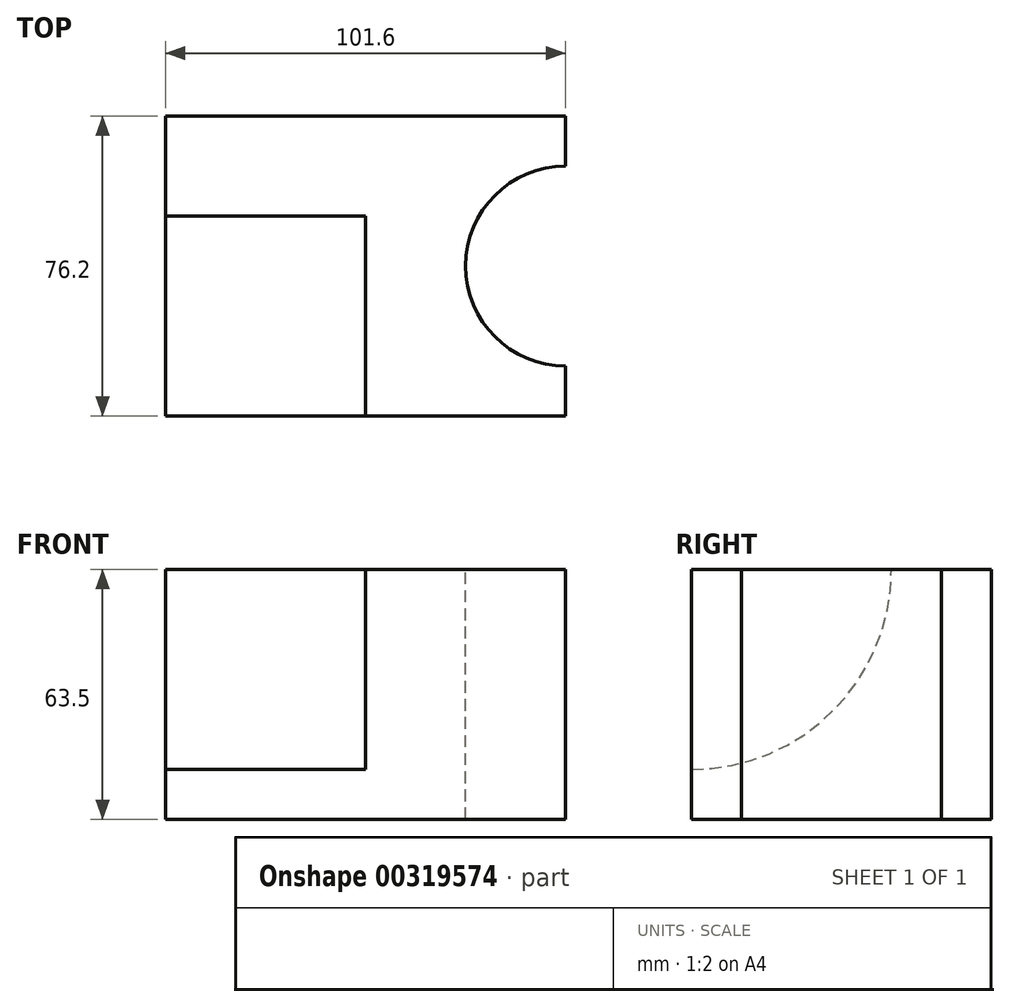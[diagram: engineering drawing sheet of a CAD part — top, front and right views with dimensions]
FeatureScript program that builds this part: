
annotation { "Feature Type Name" : "Feature", "Feature Type Description" : "" }
export const myFeature = defineFeature(function(context is Context, id is Id, definition is map)
    precondition{}
    {
        {
            var Q0;
            Q0=qCreatedBy(makeId("Front.planeOp"),FACE);
            var sketch = newSketch(context, id + "F0", { "sketchPlane" : qUnion([Q0])});
            skLineSegment(sketch, "E0", {"start": v(-45.54, -62.06) * mm, "end": v(56.06, -62.06) * mm});
            skLineSegment(sketch, "E1", {"start": v(-45.54, -62.06) * mm, "end": v(-45.54, 1.44) * mm});
            skLineSegment(sketch, "E2", {"start": v(-45.54, 1.44) * mm, "end": v(56.06, 1.44) * mm});
            skLineSegment(sketch, "E3", {"start": v(56.06, 1.44) * mm, "end": v(56.06, -62.06) * mm});
            skSolve(sketch);
        }
        {
            var Q0;
            Q0=makeQuery(id+"F0.imprint","IMPRINT",FACE,{"disambiguationData":[TD([[makeQuery(id+"F0.imprint","IMPRINT",EDGE,{"derivedFrom":sQuery(id+"F0.wireOp",EDGE,"E0")}),1.0]])]});
            extrude(context, id + "F1", {"entities" : qUnion([Q0]), "depth" : 76.2 * mm});
        }
        {
            var Q0;
            Q0=makeQuery(id+"F1.opExtrude","SWEPT_FACE",FACE,{"disambiguationData":[OSD([sQuery(id+"F0.wireOp",EDGE,"E2")])]});
            var sketch = newSketch(context, id + "F2", { "sketchPlane" : qUnion([Q0])});
            skArc(sketch, "E4", {"start": v(56.06, -12.7) * mm, "mid": v(30.66, -38.1) * mm, "end": v(56.06, -63.5) * mm});
            skLineSegment(sketch, "E5", {"start": v(56.06, -63.5) * mm, "end": v(56.06, -12.7) * mm});
            skSolve(sketch);
        }
        {
            var Q0;
            Q0=makeQuery(id+"F2.imprint","IMPRINT",FACE,{"disambiguationData":[TD([[makeQuery(id+"F2.imprint","IMPRINT",EDGE,{"derivedFrom":sQuery(id+"F2.wireOp",EDGE,"E4")}),1.0]])]});
            extrude(context, id + "F3", {"entities" : qUnion([Q0]), "operationType" : NewBodyOperationType.REMOVE, "oppositeDirection" : true, "depth" : 63.5 * mm});
        }
        {
            var Q0;
            Q0=makeQuery(id+"F1.opExtrude","SWEPT_FACE",FACE,{"disambiguationData":[OSD([sQuery(id+"F0.wireOp",EDGE,"E1")])]});
            var sketch = newSketch(context, id + "F4", { "sketchPlane" : qUnion([Q0])});
            skArc(sketch, "E6", {"start": v(25.4, 1.44) * mm, "mid": v(40.28, -34.48) * mm, "end": v(76.2, -49.36) * mm});
            skLineSegment(sketch, "E7", {"start": v(76.2, 1.44) * mm, "end": v(25.4, 1.44) * mm});
            skLineSegment(sketch, "E8", {"start": v(76.2, 1.44) * mm, "end": v(76.2, -49.36) * mm});
            skSolve(sketch);
        }
        {
            var Q0;
            Q0=makeQuery(id+"F4.imprint","IMPRINT",FACE,{"disambiguationData":[TD([[makeQuery(id+"F4.imprint","IMPRINT",EDGE,{"derivedFrom":sQuery(id+"F4.wireOp",EDGE,"E6")}),1.0]])]});
            extrude(context, id + "F5", {"entities" : qUnion([Q0]), "operationType" : NewBodyOperationType.REMOVE, "oppositeDirection" : true, "depth" : 50.8 * mm});
        }
    });
